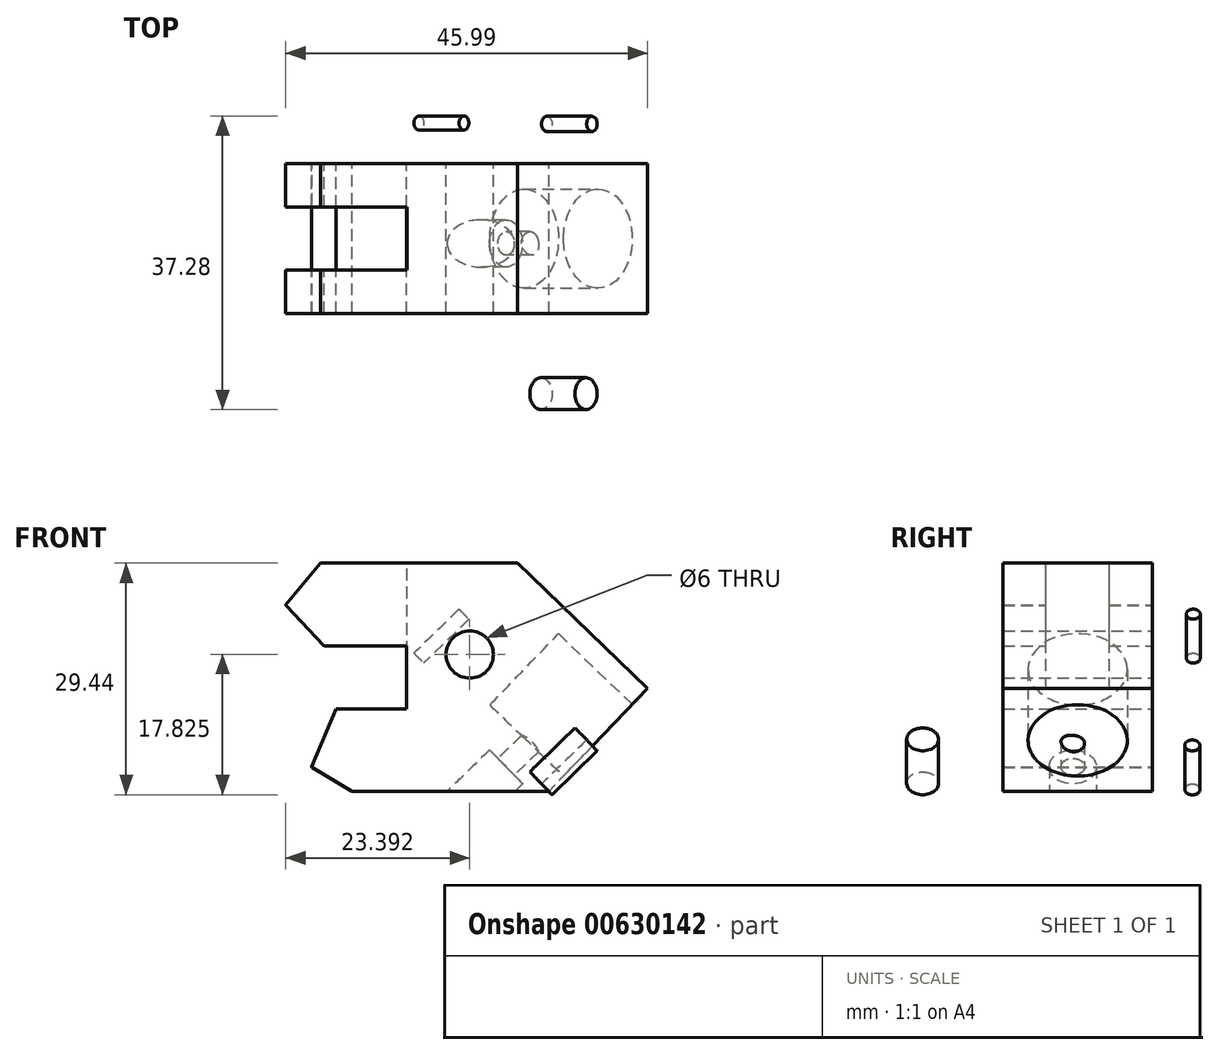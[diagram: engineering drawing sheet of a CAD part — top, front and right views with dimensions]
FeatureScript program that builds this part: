
annotation { "Feature Type Name" : "Feature", "Feature Type Description" : "" }
export const myFeature = defineFeature(function(context is Context, id is Id, definition is map)
    precondition{}
    {
        {
            var Q0;
            Q0=qCreatedBy(makeId("Front.planeOp"),FACE);
            var sketch = newSketch(context, id + "F0", { "sketchPlane" : qUnion([Q0])});
            skLineSegment(sketch, "E0", {"start": v(-71.85, 9.4) * mm, "end": v(-46.85, 9.4) * mm});
            skLineSegment(sketch, "E1", {"start": v(-67.85, -19.6) * mm, "end": v(-42.85, -19.6) * mm});
            skLineSegment(sketch, "E2", {"start": v(-46.85, 9.4) * mm, "end": v(-30.29, -6.55) * mm});
            skLineSegment(sketch, "E3", {"start": v(-30.29, -6.55) * mm, "end": v(-42.85, -19.6) * mm});
            skLineSegment(sketch, "E4", {"start": v(-60.89, -1.1) * mm, "end": v(-60.89, -9.1) * mm});
            skLineSegment(sketch, "E5", {"start": v(-71.39, -1.1) * mm, "end": v(-60.89, -1.1) * mm});
            skLineSegment(sketch, "E6", {"start": v(-69.89, -9.1) * mm, "end": v(-60.89, -9.1) * mm});
            skArc(sketch, "E7", {"start": v(-76.28, 4.05) * mm, "mid": v(-76.27, 4.04) * mm, "end": v(-76.25, 4.02) * mm});
            skArc(sketch, "E8", {"start": v(-76.25, 4.02) * mm, "mid": v(-76.25, 4.02) * mm, "end": v(-76.25, 4.02) * mm});
            skLineSegment(sketch, "E9", {"start": v(-71.85, 9.4) * mm, "end": v(-76.28, 4.05) * mm});
            skLineSegment(sketch, "E10", {"start": v(-76.28, 4.05) * mm, "end": v(-71.39, -1.1) * mm});
            skArc(sketch, "E11", {"start": v(-73, -16.52) * mm, "mid": v(-72.96, -16.53) * mm, "end": v(-72.93, -16.54) * mm});
            skArc(sketch, "E12", {"start": v(-72.93, -16.54) * mm, "mid": v(-72.93, -16.55) * mm, "end": v(-72.94, -16.55) * mm});
            skLineSegment(sketch, "E13", {"start": v(-69.89, -9.1) * mm, "end": v(-73, -16.52) * mm});
            skLineSegment(sketch, "E14", {"start": v(-73, -16.52) * mm, "end": v(-67.85, -19.6) * mm});
            skCircle(sketch, "E15", {"center": v(-52.89, -2.22) * mm, "radius": 3 * mm});
            skSolve(sketch);
        }
        {
            var Q0;
            Q0=makeQuery(id+"F0.imprint","IMPRINT",FACE,{"disambiguationData":[TD([[makeQuery(id+"F0.imprint","IMPRINT",EDGE,{"derivedFrom":sQuery(id+"F0.wireOp",EDGE,"E0")}),-1.0]])]});
            extrude(context, id + "F1", {"entities" : qUnion([Q0]), "depth" : 19 * mm});
        }
        {
            var Q0;
            Q0=makeQuery(id+"F1.opExtrude","SWEPT_FACE",FACE,{"disambiguationData":[OSD([sQuery(id+"F0.wireOp",EDGE,"E0")])]});
            var sketch = newSketch(context, id + "F2", { "sketchPlane" : qUnion([Q0])});
            skLineSegment(sketch, "E16", {"start": v(-29.52, -5.5) * mm, "end": v(-97.4, -5.5) * mm});
            skLineSegment(sketch, "E17", {"start": v(-28.86, -13.5) * mm, "end": v(-100.5, -13.5) * mm});
            skLineSegment(sketch, "E18", {"start": v(-97.4, -5.5) * mm, "end": v(-97.4, -13.5) * mm});
            skLineSegment(sketch, "E19", {"start": v(-60.85, -5.5) * mm, "end": v(-60.85, -13.5) * mm});
            skSolve(sketch);
        }
        {
            var Q0;
            {var subQ0=sQuery(id+"F2.wireOp",EDGE,"E19");Q0=makeQuery(id+"F2.imprint","IMPRINT",FACE,{"disambiguationData":[TD([[makeQuery(id+"F2.imprint","IMPRINT",EDGE,{"derivedFrom":subQ0}),-1.0]])]});}
            var Q1;
            {var subQ0=sQuery(id+"F2.wireOp",EDGE,"E18");Q1=makeQuery(id+"F2.imprint","IMPRINT",FACE,{"disambiguationData":[TD([[makeQuery(id+"F2.imprint","IMPRINT",EDGE,{"derivedFrom":subQ0}),1.0]])]});}
            extrude(context, id + "F3", {"entities" : qUnion([Q0, Q1]), "operationType" : NewBodyOperationType.REMOVE, "oppositeDirection" : true, "depth" : 16 * mm});
        }
        {
            var Q0;
            Q0=makeQuery(id+"F1.opExtrude","SWEPT_FACE",FACE,{"disambiguationData":[OSD([sQuery(id+"F0.wireOp",EDGE,"E3")])]});
            var sketch = newSketch(context, id + "F4", { "sketchPlane" : qUnion([Q0])});
            skCircle(sketch, "E20", {"center": v(-9.5, -34.85) * mm, "radius": 6.3 * mm});
            skSolve(sketch);
        }
        {
            var Q0;
            Q0=qSketchRegion(id+"F4",true);
            var Q1;
            {var subQ0=sQuery(id+"F0.wireOp",EDGE,"obgSHjAs-CF7U-fFNJ-GP6A-8ZxQo6zeKuEo");Q1=makeQuery(id+"F1.opExtrude","SWEPT_FACE",FACE,{"disambiguationData":[OSD([subQ0]),TDD([makeQuery(id+"F0.imprint","IMPRINT",EDGE,{"disambiguationData":[TD([[makeQuery(id+"F0.imprint","INTERSECT",VERTEX,{"derivedFrom":[sQuery(id+"F0.wireOp",EDGE,"E4"),subQ0]}),1.0]])],"derivedFrom":subQ0})])]});}
            extrude(context, id + "F5", {"entities" : qUnion([Q0, Q1]), "operationType" : NewBodyOperationType.REMOVE, "oppositeDirection" : true, "depth" : 13 * mm});
        }
        {
            var Q0;
            Q0=makeQuery(id+"F1.opExtrude","CAP_VERTEX",VERTEX,{"disambiguationData":[OSD([sQuery(id+"F0.wireOp",EDGE,"E1"),sQuery(id+"F0.wireOp",EDGE,"E3")])],"isStart":false});
            var Q1;
            Q1=makeQuery(id+"F1.opExtrude","CAP_VERTEX",VERTEX,{"disambiguationData":[OSD([sQuery(id+"F0.wireOp",EDGE,"E1"),sQuery(id+"F0.wireOp",EDGE,"E3")])],"isStart":true});
            var Q2;
            Q2=makeQuery(id+"F1.opExtrude","CAP_VERTEX",VERTEX,{"disambiguationData":[OSD([sQuery(id+"F0.wireOp",EDGE,"E4"),sQuery(id+"F0.wireOp",EDGE,"E5")])],"isStart":false});
            cPlane(context, id + "F6", {"entities" : qUnion([Q0, Q1, Q2]), "cplaneType" : CPlaneType.THREE_POINT, "offset" : 25 * mm, "width" : 150 * mm, "height" : 150 * mm});
        }
        {
            var Q0;
            Q0=qCreatedBy(id+"F6.planeOp",FACE);
            var sketch = newSketch(context, id + "F7", { "sketchPlane" : qUnion([Q0])});
            skCircle(sketch, "E21", {"center": v(-5.07, 16.23) * mm, "radius": 0.96 * mm});
            skCircle(sketch, "E22", {"center": v(-5.18, 39.52) * mm, "radius": 0.89 * mm});
            skCircle(sketch, "E23", {"center": v(29.2, 17.3) * mm, "radius": 2.02 * mm});
            skSolve(sketch);
        }
        {
            var Q0;
            Q0=makeQuery(id+"F7.imprint","IMPRINT",FACE,{"disambiguationData":[TD([[makeQuery(id+"F7.imprint","IMPRINT",EDGE,{"derivedFrom":sQuery(id+"F7.wireOp",EDGE,"E23")}),1.0]])]});
            var Q1;
            Q1=makeQuery(id+"F7.imprint","IMPRINT",FACE,{"disambiguationData":[TD([[makeQuery(id+"F7.imprint","IMPRINT",EDGE,{"derivedFrom":sQuery(id+"F7.wireOp",EDGE,"E21")}),1.0]])]});
            var Q2;
            Q2=makeQuery(id+"F7.imprint","IMPRINT",FACE,{"disambiguationData":[TD([[makeQuery(id+"F7.imprint","IMPRINT",EDGE,{"derivedFrom":sQuery(id+"F7.wireOp",EDGE,"E22")}),1.0]])]});
            extrude(context, id + "F8", {"entities" : qUnion([Q0, Q1, Q2]), "oppositeDirection" : true, "depth" : 8 * mm});
        }
        {
            var Q0;
            Q0=makeQuery(id+"F8.opExtrude","CAP_FACE",FACE,{"disambiguationData":[OSD([sQuery(id+"F7.wireOp",EDGE,"E23")])],"isStart":false});
            var sketch = newSketch(context, id + "F9", { "sketchPlane" : qUnion([Q0])});
            skCircle(sketch, "E24", {"center": v(-10.12, 21.9) * mm, "radius": 1.5 * mm});
            skLineSegment(sketch, "E25", {"start": v(-10.12, 15.9) * mm, "end": v(-10.12, 30.7) * mm});
            skCircle(sketch, "E26", {"center": v(-10.12, 21.9) * mm, "radius": 3 * mm});
            skPoint(sketch, "E27", {"position": v(-10.12, 23.4) * mm});
            skSolve(sketch);
        }
        {
            var Q0;
            {var subQ0=sQuery(id+"F9.wireOp",EDGE,"E25");var subQ1=sQuery(id+"F9.wireOp",EDGE,"E24");var subQ2=makeQuery(id+"F9.imprint","INTERSECT",VERTEX,{"disambiguationData":[OD(0.0)],"derivedFrom":[subQ1,subQ0]});Q0=makeQuery(id+"F9.imprint","IMPRINT",FACE,{"disambiguationData":[TD([[makeQuery(id+"F9.imprint","IMPRINT",EDGE,{"disambiguationData":[TD([[subQ2,-1.0]])],"derivedFrom":subQ1}),1.0]])]});}
            var Q1;
            {var subQ0=sQuery(id+"F9.wireOp",EDGE,"E25");var subQ1=sQuery(id+"F9.wireOp",EDGE,"E24");var subQ2=makeQuery(id+"F9.imprint","INTERSECT",VERTEX,{"disambiguationData":[OD(0.0)],"derivedFrom":[subQ1,subQ0]});Q1=makeQuery(id+"F9.imprint","IMPRINT",FACE,{"disambiguationData":[TD([[makeQuery(id+"F9.imprint","IMPRINT",EDGE,{"disambiguationData":[TD([[subQ2,1.0]])],"derivedFrom":subQ1}),1.0]])]});}
            extrude(context, id + "F10", {"entities" : qUnion([Q0, Q1]), "operationType" : NewBodyOperationType.ADD, "oppositeDirection" : true, "depth" : 25 * mm});
        }
        {
            var Q0;
            Q0=makeQuery(id+"F10.opExtrude","CAP_FACE",FACE,{"disambiguationData":[OSD([sQuery(id+"F9.wireOp",EDGE,"E24")])],"isStart":false});
            var sketch = newSketch(context, id + "F11", { "sketchPlane" : qUnion([Q0])});
            skCircle(sketch, "E28", {"center": v(10.12, 21.9) * mm, "radius": 3 * mm});
            skLineSegment(sketch, "E29", {"start": v(10.12, 21.9) * mm, "end": v(10.12, -18.39) * mm});
            skSolve(sketch);
        }
        {
            var Q0;
            Q0=makeQuery(id+"F11.imprint","IMPRINT",FACE,{"disambiguationData":[TD([[makeQuery(id+"F11.imprint","IMPRINT",EDGE,{"derivedFrom":makeQuery(id+"F10.opExtrude","CAP_EDGE",EDGE,{"disambiguationData":[OSD([sQuery(id+"F9.wireOp",EDGE,"E24")])],"isStart":false})}),-1.0]])]});
            extrude(context, id + "F12", {"entities" : qUnion([Q0]), "operationType" : NewBodyOperationType.REMOVE, "oppositeDirection" : true, "depth" : 25 * mm});
        }
        {
            var Q0;
            Q0=makeQuery(id+"F1.opExtrude","SWEPT_FACE",FACE,{"disambiguationData":[OSD([sQuery(id+"F0.wireOp",EDGE,"E1")])]});
            var sketch = newSketch(context, id + "F13", { "sketchPlane" : qUnion([Q0])});
            skLineSegment(sketch, "E30", {"start": v(-53.62, 0) * mm, "end": v(-53.62, 19) * mm});
            skPoint(sketch, "E30.startSnap0", {"position": v(-53.62, 10.12) * mm});
            skSolve(sketch);
        }
        {
            var Q0;
            Q0=sQuery(id+"F13.wireOp",VERTEX,"E30.startSnap0");
            var Q1;
            Q1=qCreatedBy(id+"F6.planeOp",FACE);
            cPlane(context, id + "F14", {"entities" : qUnion([Q0, Q1]), "cplaneType" : CPlaneType.PLANE_POINT, "offset" : 25 * mm, "width" : 150 * mm, "height" : 150 * mm});
        }
        {
            var Q0;
            Q0=qCreatedBy(id+"F14.planeOp",FACE);
            var sketch = newSketch(context, id + "F15", { "sketchPlane" : qUnion([Q0])});
            skCircle(sketch, "E31.0", {"center": v(10.12, 21.9) * mm, "radius": 1.5 * mm});
            skCircle(sketch, "E32", {"center": v(10.12, 21.9) * mm, "radius": 3 * mm});
            skSolve(sketch);
        }
        {
            var Q0;
            Q0=makeQuery(id+"F15.imprint","IMPRINT",FACE,{"disambiguationData":[TD([[makeQuery(id+"F15.imprint","IMPRINT",EDGE,{"derivedFrom":sQuery(id+"F15.wireOp",EDGE,"E31.0")}),-1.0]])]});
            extrude(context, id + "F16", {"entities" : qUnion([Q0]), "operationType" : NewBodyOperationType.REMOVE, "oppositeDirection" : true, "depth" : 6 * mm, "hasSecondDirection" : true, "secondDirectionBound" : SecondDirectionBoundingType.THROUGH_ALL, "secondDirectionOppositeDirection" : false, "secondDirectionDepth" : 0 * mm});
        }
    });
